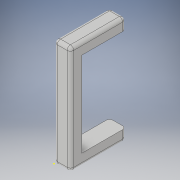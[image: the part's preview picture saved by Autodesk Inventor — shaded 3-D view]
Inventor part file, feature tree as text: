
AUTODESK INVENTOR PART (.ipt)
format: ipt  version: 2018 (Build 220112000, 112)  size: 177,152 bytes
history: native  units: in
note: dims shown in document units (in); Inventor stores cm internally (conversion verified against a paired STEP export)
features: sketch x3, extrude x2, fillet x1
ambient origin geometry x8: Origin, YZ Plane, XZ Plane, XY Plane, X Axis, Y Axis, Z Axis, Center Point
bodies: Solid1 (feature_tree)
feature tree (6):
  sketch  "Sketch1"  dims[d0=26.0in d1=13.5in d2=13.5in]
  extrude  "Extrusion1"  Depth=13.5in
  fillet  "Fillet1"  Radius=13.5in
  extrude  "Extrusion7"  Depth=3.5in
  sketch  "Sketch2"  dims[d3=3.5in d4=3.5in]
  sketch  "Sketch7"  dims[d5=3.5in d6=5.0in d7=0.0in d8=1.0in d52=0.5in d53=0.5in d54=5.0in d55=5.0in d56=5.0in d57=5.0in d58=0.375in d59=1.0in d60=1.0in d61=1.0in d62=2.0in d63=1.0in d64=2.0in d65=0.2in d66=0.375in d67=1.0in d68=0.0in]
